FCSTD DOCUMENT  (FreeCAD 0.20R29603 (Git))
Label: tc2-sim-usb-pi3-pcb
License: All rights reserved
LicenseURL: http://en.wikipedia.org/wiki/All_rights_reserved
objects: Sketcher::SketchObject×1, PartDesign::Body×1
note: 2 computed .brp shape members not serialized (recipe doc carries the construction recipe); baked Part::Feature solids carry a one-line shape summary decoded from their .brp

FEATURE [Sketcher::SketchObject] Sketch
  FullyConstrained = true
  MapMode = 5
  Support = -> [XY_Plane]
  sketch-geometry (10):
    g0: ArcOfCircle CenterX=-0.9 CenterY=5.5 CenterZ=0 NormalX=0 NormalY=0 NormalZ=1 AngleXU=0 Radius=0.5 StartAngle=1.5708 EndAngle=3.14159
    g1: LineSegment StartX=-0.9 StartY=6 StartZ=0 EndX=15.1 EndY=6 EndZ=0
    g2: ArcOfCircle CenterX=15.1 CenterY=5.5 CenterZ=0 NormalX=0 NormalY=0 NormalZ=1 AngleXU=0 Radius=0.5 StartAngle=6.948e-13 EndAngle=1.5708
    g3: LineSegment StartX=15.6 StartY=5.5 StartZ=0 EndX=15.6 EndY=-23.5 EndZ=0
    g4: ArcOfCircle CenterX=15.1 CenterY=-23.5 CenterZ=0 NormalX=0 NormalY=0 NormalZ=1 AngleXU=0 Radius=0.5 StartAngle=4.71239 EndAngle=6.28319
    g5: LineSegment StartX=15.1 StartY=-24 StartZ=0 EndX=-0.9 EndY=-24 EndZ=0
    g6: ArcOfCircle CenterX=-0.9 CenterY=-23.5 CenterZ=0 NormalX=0 NormalY=0 NormalZ=1 AngleXU=0 Radius=0.5 StartAngle=3.14159 EndAngle=4.71239
    g7: LineSegment StartX=-1.4 StartY=-23.5 StartZ=0 EndX=-1.4 EndY=5.5 EndZ=0
    g8: GeomPoint X=-1.4 Y=6 Z=0
    g9: GeomPoint X=15.6 Y=-24 Z=0
  constraints (24):
    c: Tangent(g0,g1) = 1.5708
    c: Tangent(g1,g2) = 1.5708
    c: Tangent(g2,g3) = 1.5708
    c: Tangent(g3,g4) = 1.5708
    c: Tangent(g4,g5) = 1.5708
    c: Tangent(g5,g6) = 1.5708
    c: Tangent(g6,g7) = 1.5708
    c: Tangent(g7,g0) = 1.5708
    c: Horizontal(g1)
    c: Horizontal(g5)
    c: Vertical(g3)
    c: Vertical(g7)
    c: Equal(g0,g2)
    c: Equal(g2,g4)
    c: Equal(g4,g6)
    c: PointOnObject(g8,g1)
    c: PointOnObject(g8,g7)
    c: PointOnObject(g9,g3)
    c: PointOnObject(g9,g5)
    c: Radius(g2) = 0.5
    c: DistanceX(g0,g2) = 17
    c: DistanceY(g-1,g0) = 6
    c: DistanceX(g0,g-1) = 1.4
    c: DistanceY(g4,g1) = 30
FEATURE [PartDesign::Body] Body
  Group = -> [Sketch]
  Origin = -> Origin
